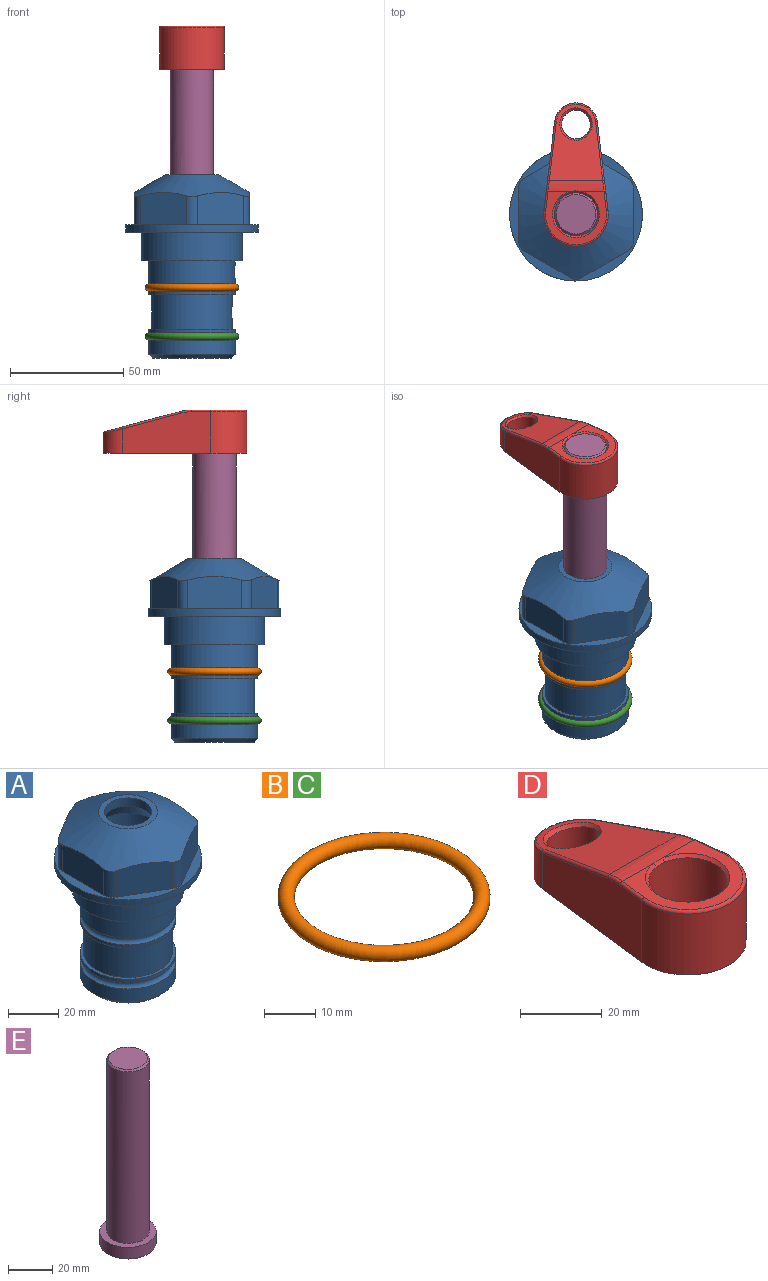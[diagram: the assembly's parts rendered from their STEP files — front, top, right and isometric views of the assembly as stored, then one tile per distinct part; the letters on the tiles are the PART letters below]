
ASSEMBLY  parts=5 mates=4
PART A: 36 faces, bbox 58.7x58.7x81 mm
  f0: cylinder r=17.78mm len=35.56mm, axis (0,0,1), area 1670.8mm2, adj f23,f24,f31
  f1: cylinder r=19.05mm len=38.1mm, axis (0,0,1), area 1191.9mm2, adj f26,f27,f30
  f2: plane 58.66x58.66mm, normal (0,0,-1), area 1150.6mm2, adj f3,f28
  f3: cylinder r=29.33mm len=58.66mm, axis (0,0,-1), area 585.1mm2, adj f2,f4
  f4: plane 58.66x58.66mm, normal (0,0,1), area 475.9mm2, adj f3,f5,f6,f7,f8,f9,f10,f11
  f5: plane 20.32x14.34mm, normal (-0.5,0.87,0), area 324.4mm2, adj f4,f15,f16,f17
  f6: plane 20.32x14.34mm, normal (0.5,0.87,0), area 324.4mm2, adj f4,f14,f15,f17
  f7: plane 23.48x14.34mm, normal (1,0,0), area 324.4mm2, adj f4,f13,f14,f17
  f8: plane 20.32x14.34mm, normal (0.5,-0.87,0), area 324.4mm2, adj f4,f12,f13,f17
  f9: plane 20.32x14.34mm, normal (-0.5,-0.87,0), area 324.4mm2, adj f4,f11,f12,f17
  f10: plane 23.48x14.34mm, normal (-1,0,0), area 324.4mm2, adj f4,f11,f16,f17
  f11: cylinder r=5.08mm len=12.85mm, axis (0,0,-1), area 67.2mm2, adj f4,f9,f10,f17
  f12: cylinder r=5.08mm len=12.85mm, axis (0,0,-1), area 67.2mm2, adj f4,f8,f9,f17
  f13: cylinder r=5.08mm len=12.85mm, axis (0,0,-1), area 67.2mm2, adj f4,f7,f8,f17
  f14: cylinder r=5.08mm len=12.85mm, axis (0,0,-1), area 67.2mm2, adj f4,f6,f7,f17
  f15: cylinder r=5.08mm len=12.85mm, axis (0,0,-1), area 67.2mm2, adj f4,f5,f6,f17
  f16: cylinder r=5.08mm len=12.85mm, axis (0,0,-1), area 67.2mm2, adj f4,f5,f10,f17
  f17: cone r=11.73mm half-angle=60deg, axis (0,0,-1), area 2071.8mm2, adj f5,f6,f7,f8,f9,f10,f11,f12
  f18: plane 23.46x23.46mm, normal (0,0,1), area 147.4mm2, adj f17,f35
  f19: plane 34.93x34.93mm, normal (0,0,-1), area 958mm2, adj f29
  f20: cylinder r=19.05mm len=38.1mm, axis (0,0,1), area 760.1mm2, adj f21,f29
  f21: torus R=19.05mm, axis (0,0,1), area 565.3mm2, adj f20,f22
  f22: cylinder r=19.05mm len=38.1mm, axis (0,0,1), area 190mm2, adj f21,f23
  f23: plane 38.1x38.1mm, normal (0,0,1), area 146.9mm2, adj f0,f22
  f24: plane 38.1x38.1mm, normal (0,0,-1), area 146.9mm2, adj f0,f25
  f25: cylinder r=19.05mm len=38.1mm, axis (0,0,1), area 190mm2, adj f24,f26
  f26: torus R=19.05mm, axis (0,0,1), area 565.3mm2, adj f1,f25
  f27: plane 44.45x44.45mm, normal (0,0,-1), area 411.7mm2, adj f1,f28
  f28: cylinder r=22.23mm len=44.45mm, axis (0,0,1), area 1773.5mm2, adj f2,f27
  f29: cone r=19.05mm half-angle=45deg, axis (0,0,1), area 257.5mm2, adj f19,f20
  f30: cylinder r=3.17mm len=6.75mm, axis (-1,0,0), area 128mm2, adj f1,f33
  f31: cylinder r=3.17mm len=6.35mm, axis (-1,0,0), area 102.5mm2, adj f0,f33
  f32: plane 25.4x25.4mm, normal (0,0,1), area 506.7mm2, adj f33
  f33: cylinder r=12.7mm len=66.42mm, axis (0,0,-1), area 5236.2mm2, adj f30,f31,f32,f34
  f34: cone r=9.53mm half-angle=30deg, axis (0,0,-1), area 443.4mm2, adj f33,f35
  f35: cylinder r=9.53mm len=19.05mm, axis (0,0,-1), area 240.9mm2, adj f18,f34
PART B: 1 faces, bbox 44.7x44.7x3.2 mm
  f0: torus R=19.05mm, axis (0,0,1), area 1193.9mm2
PART C: same geometry as B
PART D: 31 faces, bbox 31.7x65.5x19.8 mm
  f0: plane 39.12x18.26mm, normal (0.99,0.12,0), area 612.2mm2, adj f1,f4,f7,f11,f13,f15
  f1: cylinder r=9.53mm len=18.91mm, axis (0,0,-1), area 296.1mm2, adj f0,f2,f7,f17
  f2: plane 39.12x18.26mm, normal (-0.99,0.12,0), area 612.2mm2, adj f1,f4,f7,f12,f14,f16
  f3: cylinder r=6.35mm len=12.7mm, axis (0,0,-1), area 362.4mm2, adj f7,f18
  f4: cylinder r=14.29mm len=28.58mm, axis (0,0,-1), area 882.2mm2, adj f0,f2,f7,f10
  f5: cylinder r=9.53mm len=19.05mm, axis (0,0,-1), area 1092.6mm2, adj f7,f19,f20
  f6: plane 26.99x23.69mm, normal (0,0,1), area 216.2mm2, adj f9,f10,f11,f12,f19
  f7: plane 63.5x28.58mm, normal (0,0,-1), area 661.8mm2, adj f0,f1,f2,f3,f4,f5,f22,f23
  f8: plane 33.52x23.6mm, normal (0,0.26,0.97), area 486mm2, adj f9,f15,f16,f17,f18
  f9: cylinder r=19.05mm len=24.72mm, axis (1,0,0), area 120.4mm2, adj f6,f8,f13,f14,f20
  f10: torus R=13.49mm, axis (0,0,1), area 59mm2, adj f4,f6,f11,f12
  f11: cylinder r=0.79mm len=8.67mm, axis (0.12,-0.99,0), area 10.8mm2, adj f0,f6,f10,f13
  f12: cylinder r=0.79mm len=8.67mm, axis (0.12,0.99,0), area 10.8mm2, adj f2,f6,f10,f14
  f13: bspline ~4.95x1.42mm, area 6.1mm2, adj f0,f9,f11,f15
  f14: bspline ~4.95x1.42mm, area 6.1mm2, adj f2,f9,f12,f16
  f15: cylinder r=0.79mm len=25.95mm, axis (0.12,-0.96,0.26), area 32.9mm2, adj f0,f8,f13,f17
  f16: cylinder r=0.79mm len=25.95mm, axis (0.12,0.96,-0.26), area 32.9mm2, adj f2,f8,f14,f17
  f17: bspline ~18.91x8.38mm, area 30mm2, adj f1,f8,f15,f16
  f18: bspline ~14.29x14.29mm, area 48.3mm2, adj f3,f8
  f19: cone r=9.53mm half-angle=45deg, axis (0,0,1), area 66.5mm2, adj f5,f6,f20
  f20: bspline ~3.22x0.96mm, area 3.5mm2, adj f5,f9,f19
  f21: plane 2.75x2.72mm, normal (0,0,-1), area 2.9mm2, adj f23,f25,f28
  f22: plane 23.05x15.88mm, normal (-0.99,-0.12,0), area 323.6mm2, adj f7,f25,f26,f27,f28,f29
  f23: plane 23.05x15.88mm, normal (0.99,-0.12,0), area 323.6mm2, adj f7,f21,f25,f27,f28,f30
  f24: cylinder r=9.53mm len=10.69mm, axis (0,0,-1), area 114.7mm2, adj f7,f27,f29,f30
  f25: cylinder r=12.7mm len=20.59mm, axis (0,0,-1), area 381.1mm2, adj f7,f21,f22,f23,f26,f28
  f26: plane 2.75x2.72mm, normal (0,0,-1), area 2.9mm2, adj f22,f25,f28
  f27: plane 19.72x18.37mm, normal (0,-0.26,-0.97), area 291.8mm2, adj f22,f23,f24,f28,f29,f30
  f28: cylinder r=15.88mm len=19.92mm, axis (1,0,0), area 54.8mm2, adj f21,f22,f23,f25,f26,f27
  f29: cylinder r=1.59mm len=11mm, axis (0,0,-1), area 34.7mm2, adj f7,f22,f24,f27
  f30: cylinder r=1.59mm len=11mm, axis (0,0,-1), area 34.7mm2, adj f7,f23,f24,f27
PART E: 6 faces, bbox 25.4x25.4x101.6 mm
  f0: plane 17.46x17.46mm, normal (0,0,1), area 239.5mm2, adj f5
  f1: plane 25.4x25.4mm, normal (0,0,-1), area 506.7mm2, adj f2
  f2: cylinder r=12.7mm len=25.4mm, axis (0,0,1), area 506.7mm2, adj f1,f3
  f3: plane 25.4x25.4mm, normal (0,0,1), area 221.7mm2, adj f2,f4
  f4: cylinder r=9.53mm len=94.46mm, axis (0,0,1), area 5653mm2, adj f3,f5
  f5: cone r=8.73mm half-angle=45deg, axis (0,0,-1), area 64.4mm2, adj f0,f4
PLACE A at identity fixed
PLACE B at identity
PLACE C t=(0,0,-21.59)mm
PLACE D t=(0,0,27.55)mm
PLACE E t=(0,0,27.55)mm
MATE fastened C.f0 <-> A.f0  axis (0,0,1) through (0,0,-46.1)mm
MATE cylindrical A.f0 <-> E.f2  axis (0,0,1) through (0,0,-50.55)mm
MATE fastened E.f2 <-> D.f4  axis (0,0,1) through (0,0,91.05)mm
MATE fastened B.f0 <-> A.f0  axis (0,0,1) through (0,0,-24.51)mm
